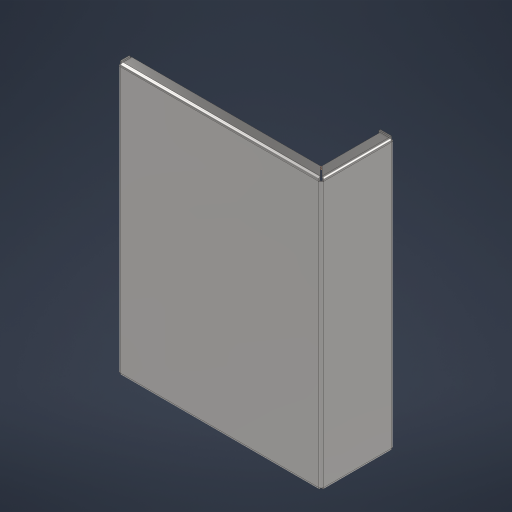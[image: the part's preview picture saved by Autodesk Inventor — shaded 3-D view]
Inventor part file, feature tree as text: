
AUTODESK INVENTOR PART (.ipt)
format: ipt  version: 2024.2 (Build 282272000, 272)  size: 601,088 bytes
history: native  units: in
note: dims shown in document units (in); Inventor stores cm internally (conversion verified against a paired STEP export)
features: sheet_metal_op x12, other x7, sketch x3, plane x2
ambient origin geometry x8: Origin, YZ Plane, XZ Plane, XY Plane, X Axis, Y Axis, Z Axis, Center Point
bodies: Solid2 (feature_tree), Solid3 (feature_tree), Solid1 (feature_tree)
feature tree (24):
  other  "HV servo drive v1_PCB.ipt"
  plane  "Work Plane1"
  sketch  "Sketch1"  dims[d0=0.3937in]
  plane  "Work Plane2"
  sheet_metal_op  "Contour Flange1"
  sheet_metal_op  "Flange1"
  sheet_metal_op  "Contour Flange2"
  sheet_metal_op  "Flange2"
  other  "Solid1::HV servo drive v1_PCB.ipt"
  other  "TaggingFeature1"
  other  "Plate1"
  sheet_metal_op  "Bend1"
  sheet_metal_op  "Corner1"
  sketch  "Sketch2"  dims[d1=0.0625in]
  other  "Plate2"
  sheet_metal_op  "Bend2"
  sheet_metal_op  "Corner2"
  other  "Plate3"
  sheet_metal_op  "Bend3"
  sheet_metal_op  "Corner3"
  sketch  "Sketch3"  dims[d2=0.3in d3=0.25in d4=0.2in d7=0.0625in d8=0.0394in d9=0.0394in d10=0.0197in d11=0.0787in d12=0.0394in d13=8.0in d14=0.0394in d15=0.039in d16=0.1575in d17=0.0394in d18=0.0394in d20=1.7717in d21=0.01in d22=0.0394in d23=0.0197in d24=0.0787in d25=0.0394in d26=0.3in d27=90.0deg d28=0.0394in d29=0.1575in d30=0.0394in d31=0.0394in d32=0.0394in d33=0.0394in d34=0.0787in d35=0.0787in d36=0.0394in d37=0.0394in d38=0.0197in d39=0.0787in d40=0.0394in d41=8.0in d42=0.0394in d43=0.039in d44=0.1575in d45=0.0394in d46=0.0394in d47=0.0394in d48=0.0197in d49=0.0787in d50=0.0394in d51=0.3in d52=90.0deg d53=0.0394in d54=0.0in d55=0.1575in d56=0.0394in d57=0.0394in]
  other  "Plate4"
  sheet_metal_op  "Bend4"
  sheet_metal_op  "Corner4"
